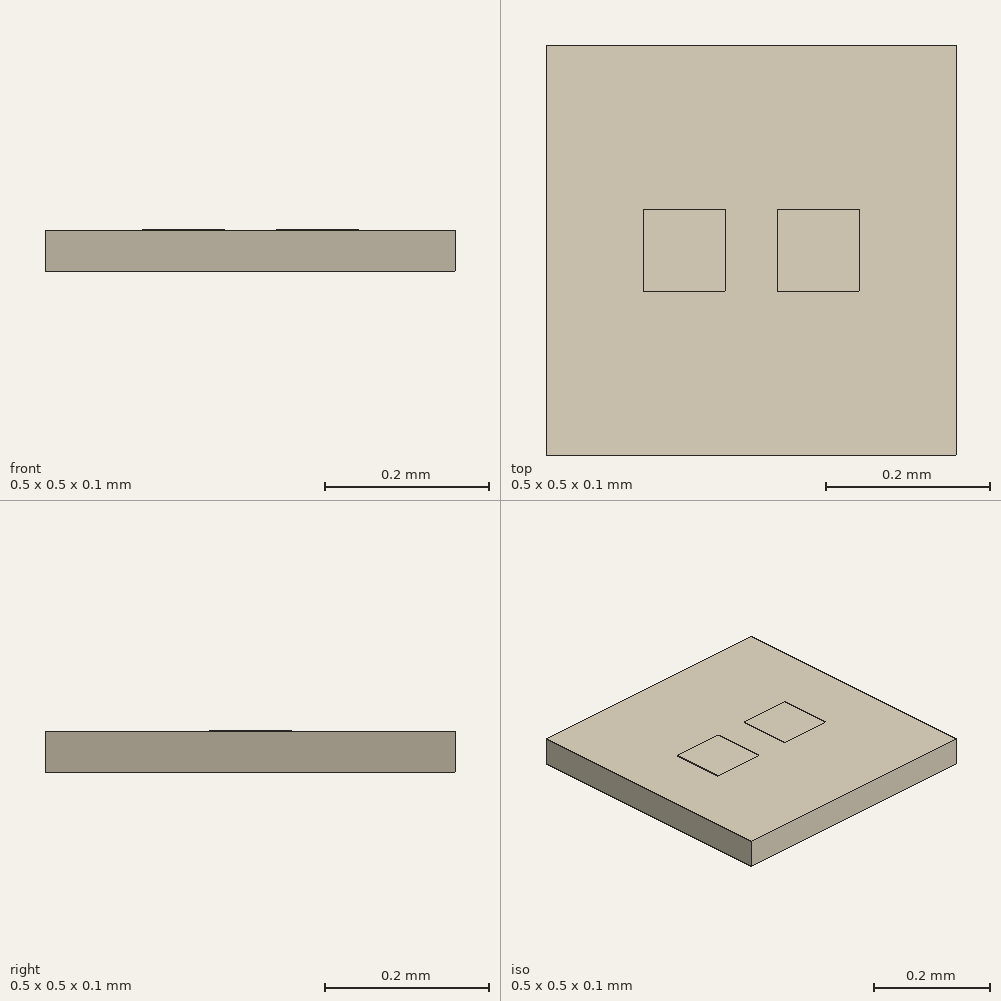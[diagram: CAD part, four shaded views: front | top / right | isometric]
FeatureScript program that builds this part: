
annotation { "Feature Type Name" : "Feature", "Feature Type Description" : "" }
export const myFeature = defineFeature(function(context is Context, id is Id, definition is map)
    precondition{}
    {
        {
            var Q0;
            Q0=qCreatedBy(makeId("Top.planeOp"),FACE);
            var sketch = newSketch(context, id + "F0", { "sketchPlane" : qUnion([Q0])});
            skLineSegment(sketch, "E0.bottom", {"start": v(0.25, 0.25) * mm, "end": v(-0.25, 0.25) * mm});
            skLineSegment(sketch, "E0.top", {"start": v(0.25, -0.25) * mm, "end": v(-0.25, -0.25) * mm});
            skLineSegment(sketch, "E0.left", {"start": v(0.25, 0.25) * mm, "end": v(0.25, -0.25) * mm});
            skLineSegment(sketch, "E0.right", {"start": v(-0.25, 0.25) * mm, "end": v(-0.25, -0.25) * mm});
            skPoint(sketch, "E0.middle", {"position": v(0, 0) * mm});
            skSolve(sketch);
        }
        {
            var Q0;
            Q0 = qSketchRegion(id + "F0", true);
            extrude(context, id + "F1", {"entities" : qUnion([Q0]), "depth" : 0.05 * mm, "offsetDistance" : 25 * mm});
        }
        {
            var Q0;
            Q0=makeQuery(id+"F1.opExtrude","CAP_FACE",FACE,{"disambiguationData":[OSD([sQuery(id+"F0.wireOp",EDGE,"E0.bottom"),sQuery(id+"F0.wireOp",EDGE,"E0.top"),sQuery(id+"F0.wireOp",EDGE,"E0.left"),sQuery(id+"F0.wireOp",EDGE,"E0.right")])],"isStart":false});
            var sketch = newSketch(context, id + "F2", { "sketchPlane" : qUnion([Q0])});
            skLineSegment(sketch, "E1.bottom", {"start": v(0.13, 0.05) * mm, "end": v(0.03, 0.05) * mm});
            skLineSegment(sketch, "E1.top", {"start": v(0.13, -0.05) * mm, "end": v(0.03, -0.05) * mm});
            skLineSegment(sketch, "E1.left", {"start": v(0.13, 0.05) * mm, "end": v(0.13, -0.05) * mm});
            skLineSegment(sketch, "E1.right", {"start": v(0.03, 0.05) * mm, "end": v(0.03, -0.05) * mm});
            skPoint(sketch, "E1.middle", {"position": v(0.08, 0) * mm});
            skLineSegment(sketch, "E2.bottom", {"start": v(-0.13, 0.05) * mm, "end": v(-0.03, 0.05) * mm});
            skLineSegment(sketch, "E2.top", {"start": v(-0.13, -0.05) * mm, "end": v(-0.03, -0.05) * mm});
            skLineSegment(sketch, "E2.left", {"start": v(-0.13, 0.05) * mm, "end": v(-0.13, -0.05) * mm});
            skLineSegment(sketch, "E2.right", {"start": v(-0.03, 0.05) * mm, "end": v(-0.03, -0.05) * mm});
            skPoint(sketch, "E2.middle", {"position": v(-0.08, 0) * mm});
            skSolve(sketch);
        }
        {
            var Q0;
            Q0 = qSketchRegion(id + "F2", true);
            extrude(context, id + "F3", {"entities" : qUnion([Q0]), "operationType" : NewBodyOperationType.ADD, "depth" : 0 * mm, "offsetDistance" : 25 * mm});
        }
    });
